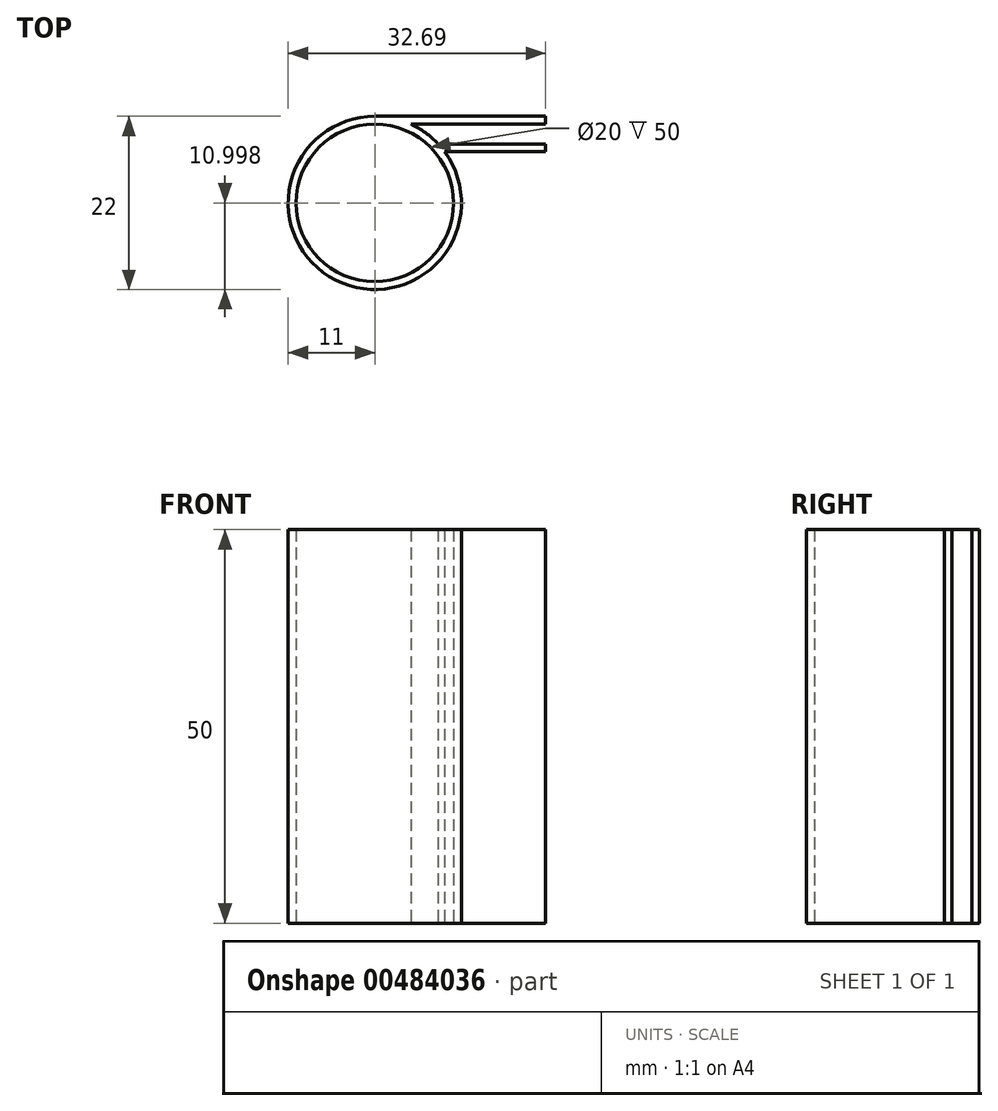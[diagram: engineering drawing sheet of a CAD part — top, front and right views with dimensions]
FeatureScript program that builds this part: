
annotation { "Feature Type Name" : "Feature", "Feature Type Description" : "" }
export const myFeature = defineFeature(function(context is Context, id is Id, definition is map)
    precondition{}
    {
        {
            var Q0;
            Q0=qCreatedBy(makeId("Top.planeOp"),FACE);
            var sketch = newSketch(context, id + "F0", { "sketchPlane" : qUnion([Q0])});
            skCircle(sketch, "E0", {"center": v(-21.7, 11.7) * mm, "radius": 10 * mm});
            skArc(sketch, "E1", {"start": v(-13.64, 19.2) * mm, "mid": v(-15.25, 20.63) * mm, "end": v(-17.1, 21.7) * mm});
            skLineSegment(sketch, "E2.bottom", {"start": v(-21.7, 22.7) * mm, "end": v(0, 22.7) * mm});
            skLineSegment(sketch, "E2.top", {"start": v(-17.1, 21.7) * mm, "end": v(0, 21.7) * mm});
            skLineSegment(sketch, "E2.right", {"start": v(0, 22.7) * mm, "end": v(0, 21.7) * mm});
            skLineSegment(sketch, "E3.bottom", {"start": v(-13.64, 19.2) * mm, "end": v(0, 19.2) * mm});
            skLineSegment(sketch, "E3.top", {"start": v(-12.82, 18.2) * mm, "end": v(0, 18.2) * mm});
            skLineSegment(sketch, "E3.right", {"start": v(0, 19.2) * mm, "end": v(0, 18.2) * mm});
            skPoint(sketch, "E3.left.start.orphan", {"position": v(-21.7, 19.2) * mm});
            skPoint(sketch, "E2.left.end.orphan", {"position": v(-21.7, 21.7) * mm});
            skArc(sketch, "E4.trimOffspring", {"start": v(-21.7, 22.7) * mm, "mid": v(-26.67, 1.9) * mm, "end": v(-12.82, 18.2) * mm});
            skSolve(sketch);
        }
        {
            var Q0;
            Q0 = qSketchRegion(id + "FeUH7nqYtj7zyHl_0", true);
            var Q1;
            Q1=makeQuery(id+"F0.imprint","IMPRINT",FACE,{"disambiguationData":[TD([[makeQuery(id+"F0.imprint","IMPRINT",EDGE,{"derivedFrom":sQuery(id+"F0.wireOp",EDGE,"E0")}),1.0]])]});
            var Q2;
            Q2=makeQuery(id+"F0.imprint","IMPRINT",FACE,{"disambiguationData":[TD([[makeQuery(id+"F0.imprint","IMPRINT",EDGE,{"derivedFrom":sQuery(id+"F0.wireOp",EDGE,"E0")}),-1.0]])]});
            extrude(context, id + "F1", {"entities" : qUnion([Q0, Q1, Q2]), "depth" : 50 * mm});
        }
        {
            var Q0;
            Q0=sQuery(id+"F0.wireOp",VERTEX,"E0.center");
            var Q1;
            Q1=makeQuery(id+"F1.opExtrude","SWEPT_BODY",BODY,{"disambiguationData":[OSD([sQuery(id+"F0.wireOp",EDGE,"E1"),sQuery(id+"F0.wireOp",EDGE,"E2.bottom"),sQuery(id+"F0.wireOp",EDGE,"E2.top"),sQuery(id+"F0.wireOp",EDGE,"E2.right"),sQuery(id+"F0.wireOp",EDGE,"E3.bottom"),sQuery(id+"F0.wireOp",EDGE,"E3.top"),sQuery(id+"F0.wireOp",EDGE,"E3.right"),sQuery(id+"F0.wireOp",EDGE,"E4.trimOffspring")])]});
            hole(context, id + "F2", {"style" : HoleStyle.SIMPLE, "endStyle" : HoleEndStyle.BLIND, "oppositeDirection" : true, "holeDiameter" : 20 * mm, "holeDepth" : 51 * mm, "isTappedThrough" : true, "tappedDepth" : 12 * mm, "tapClearance" : 3, "startFromSketch" : true, "locations" : qUnion([Q0]), "scope" : qUnion([Q1])});
        }
    });
